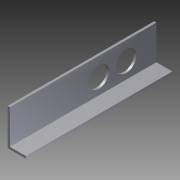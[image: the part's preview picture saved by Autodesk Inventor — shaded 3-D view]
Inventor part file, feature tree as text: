
AUTODESK INVENTOR PART (.ipt)
format: ipt  version: 2012 (Build 160160000, 160)  size: 91,136 bytes
history: native  units: in
note: dims shown in document units (in); Inventor stores cm internally (conversion verified against a paired STEP export)
features: extrude x2, sketch x2
ambient origin geometry x8: Origin, YZ Plane, XZ Plane, XY Plane, X Axis, Y Axis, Z Axis, Center Point
bodies: Solid1 (feature_tree)
feature tree (4):
  extrude  "Extrusion1"  Depth=1.0in
  extrude  "Extrusion2"  Depth=0.125in
  sketch  "Sketch1"  dims[d0=2.0in d1=1.0in]
  sketch  "Sketch2"  dims[d2=0.125in d3=0.125in d4=8.0in d5=0.0in d6=1.125in d7=1.125in d8=1.0in d10=1.5in d11=8.0in d12=0.0in d13=1.65in]
